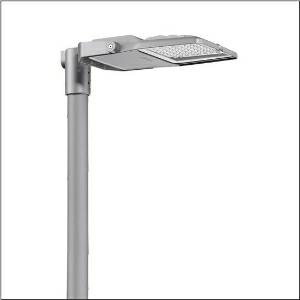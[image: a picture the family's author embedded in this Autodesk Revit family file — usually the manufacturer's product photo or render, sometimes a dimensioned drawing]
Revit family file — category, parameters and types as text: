
# Revit family: floodlight_fl_21_iq_mini___pl33t_5xa7771b4f3a_1cb2
name_source: partatom
category: Lighting Fixtures
units: mm (PartAtom-declared; Revit-internal decimal feet)

## family parameters
Cut with Voids When Loaded = No
Host = Face
Light Source = No
Part Type = Normal
Room Calculation Point = No
Round Connector Dimension = Use Diameter
Shared = No

## types (1)
- --- (1 x LED, 6420 lm, 45.5 W, 4000K)
    Apparent Load = 46 VA
    CIE Flux Codes = 26 75 99 100 100
    Color Rendering = 70
    Color Temperature = 4000K
    Default Elevation = 1800 mm
    Description = Floodlight FL 21 iQ mini, floodlight, primary light control with lens, of PMMA, primary optical cover: protective disc, of toughened safety glass, transparent, light distribution: PL33T, light emission: direct distribution, installation type: surface-mounted, LED, High Power LED, rated luminous flux: 6.420lm, luminous efficacy: 141lm/W, light colour: 740, colour temperature: 4000K, control gear: iQ Comfort/DALI, control: Auto-Match, Temp-Guard, Lumen-Switch, Night-Set, Smart-Wire, Light-Fading, Desk-Remote (wireless, voltage-free reading and setting of iQ features in the workshop via application-optimized NFC function/RFID function), optimised constant luminous flux control (CLO 2.0), with terminal, 6-pole, mains connection: 220..240V, AC, 50/60Hz, start of lifetime: 46W, end of service life: 48W, reduction: 22W, luminaire housing, of diecast aluminium, powder-coated, Siteco® metallic grey (DB 702S), corrosivity category C5 mid according to DIN EN ISO 12944, suitable for swimming pools, chlorine-resistant, sealing non-destructively replaceable, please order mast flange separately, mast bracket, of steel, galvanised, powder-coated, Siteco® metallic grey (DB 702S), protection rating (complete): IP66, insulation class (complete): insulation class II (safety insulation), certification: CE, ENEC, VDE, protection symbol: D, impact resistance: IK08, permissible operating ambient temperature: -40..+40°C, permissible operating ambient temperature for outdoor applications: -40..+50°C, standard: DIN EN 12944, LABS conformity tested according to VDMA 24364:2018-05, packaging unit: 1 piece

Light Distribution: PL33T
    Height = 70 mm
    Lamp = 1 x LED
    Lamp Light Flux = 6420 lm
    Lamp Power = 45.5 W
    Lamp count = 1
    Length = 485 mm
    Luminous efficacy = 141 lm/W
    Manufacturer = Siteco
    ModVariant = No
    Model = 5XA7771B4F3A
    Number of Poles = 1
    OnlyDefault = Yes
    Power Factor = 1
    Product Name = Floodlight FL 21 iQ mini | PL33T
    Product group = floodlight | pylon annexe
    ProductGroupID = 6201
    Protection Class = Protection class II
    Protection Degree = IP 66
    RLX_Detail_Level = 1
    RLX_Emergency_Light_Flux = 0 lm
    RLX_Emergency_Type = 0
    RLX_Emergency_Type_DB = No
    RlxData = <blob elided: 101161 chars, md5=b449e706>
    Socket = socket
    Standby Power = 0 W
    System Light Flux = 6420 lm
    System Power = 46 W
    Type Comments = factory setting: luminous flux: 100 % | dim-lin: 254 | 463 mA
    Type Image = l_1007125.jpg
    URL = http://relux.com
    VarID = @adj_171617
    Voltage = 0 V
    Weight = 0.00 kg
    Width = 337 mm

## geometry (parser evidence)
native form markers: Blend x4, Sweep x12
no freeform markers — native parametric forms only
